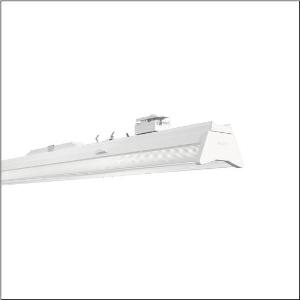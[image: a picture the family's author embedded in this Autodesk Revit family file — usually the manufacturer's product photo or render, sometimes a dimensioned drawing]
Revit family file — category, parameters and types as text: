
# Revit family: licross_11_performance_tw_51td16tnt85x
name_source: partatom
category: Lighting Fixtures
units: mm (PartAtom-declared; Revit-internal decimal feet)

## family parameters
Cut with Voids When Loaded = No
Host = Face
Light Source = No
Part Type = Normal
Room Calculation Point = No
Round Connector Dimension = Use Diameter
Shared = No

## types (1)
- --- (1 x LED 2700 K ... 6500 K, 8930 lm, 56 W, 2700K)
    Apparent Load = 56 VA
    CIE Flux Codes = 63 87 95 78 100
    Color Rendering = 80
    Color Temperature = 2700K
    Default Elevation = 1800 mm
    Description = Licross 11 Performance TW, luminaire insert, of sheet steel, galvanised, coil coated, white, length: 1.500mm, width: 120mm, height: 123mm, LED rated luminous flux: 8.930lm, light colour: 8tw, SDCM (Standard Deviation of Colour Matching)MacAdam ≤ 2 SDCM (initial), control gear: DALI DT8, with plug, 5-pole, with phase selection, mains connection: 220..240V, AC, 50/60Hz, rated input power: 56W, internal wiring halogen-free, primary light control with lens, of plastic, primary optical cover: cover, of PMMA, light emission: direct/indirect distribution, primary light characteristic: symmetric, protection rating (complete): IP54, insulation class (complete): insulation class I (protective earthing), certification: CE, ENEC, VDE, UKCA, protection symbol: D if used in an environment with non-conductive dust loads with corresponding accessories, impact resistance: IK06, permissible ambient temperature for indoor applications: -25..+35°C, corresponds to IFS (International Featured Standards) requirements for safety and quality in the food industry, reducing of maximum allowable ambient temperature of 5°C with ceiling mounting, LABS conformity tested according to VDMA 24364:2018-05, The light source and the operating device comply with the requirements of the Ecodesign Regulation (EU) 2019/2020 and are replaceable in accordance with this regulation, packaging unit: 1 piece
    Height = 114 mm
    Lamp = 1 x LED 2700 K ... 6500 K
    Lamp Light Flux = 8930 lm
    Lamp Power = 56 W
    Lamp count = 1
    Length = 1500 mm
    Luminous efficacy = 159 lm/W
    Manufacturer = Siteco
    ModVariant = No
    Model = 51TD16TNT85X
    Mounting Place = Ceiling
    Mounting Type = Pendant
    Number of Poles = 1
    OnlyDefault = Yes
    Power Factor = 1
    Product Name = Licross 11 Performance TW
    Product group = luminaire insert | ceiling pendant
    ProductGroupID = 901
    Protection Class = Protection class I
    Protection Degree = IP 54
    RLX_Detail_Level = 1
    RLX_Emergency_Light_Flux = 0 lm
    RLX_Emergency_Type = 0
    RLX_Emergency_Type_DB = No
    RlxData = <blob elided: 30717 chars, md5=abb639ab>
    Socket = socket
    Standby Power = 0 W
    System Light Flux = 8930 lm
    System Power = 56 W
    Type Comments = individual setting: CCT=2700K
    Type Image = l_1256138.jpg
    URL = http://relux.com
    VarID = @adj_057925
    Voltage = 0 V
    Weight = 0.00 kg
    Width = 120 mm

## geometry (parser evidence)
native form markers: Blend x4, Sweep x12
no freeform markers — native parametric forms only
